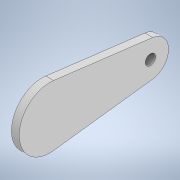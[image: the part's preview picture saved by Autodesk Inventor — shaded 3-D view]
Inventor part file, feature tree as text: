
AUTODESK INVENTOR PART (.ipt)
format: ipt  version: 2020 (Build 240168000, 168)  size: 142,336 bytes
history: native  units: mm
features: sketch x3, extrude x1, projected_geometry x1
ambient origin geometry x8: Origin, YZ Plane, XZ Plane, XY Plane, X Axis, Y Axis, Z Axis, Center Point
bodies: Body1 (feature_tree)
feature tree (5):
  extrude  "Выдавливание4"  Depth=18.6mm
  sketch  "Эскиз4"
  sketch  "Эскиз5"
  sketch  "Эскиз1"
  projected_geometry  "Спроецированная петля3"
